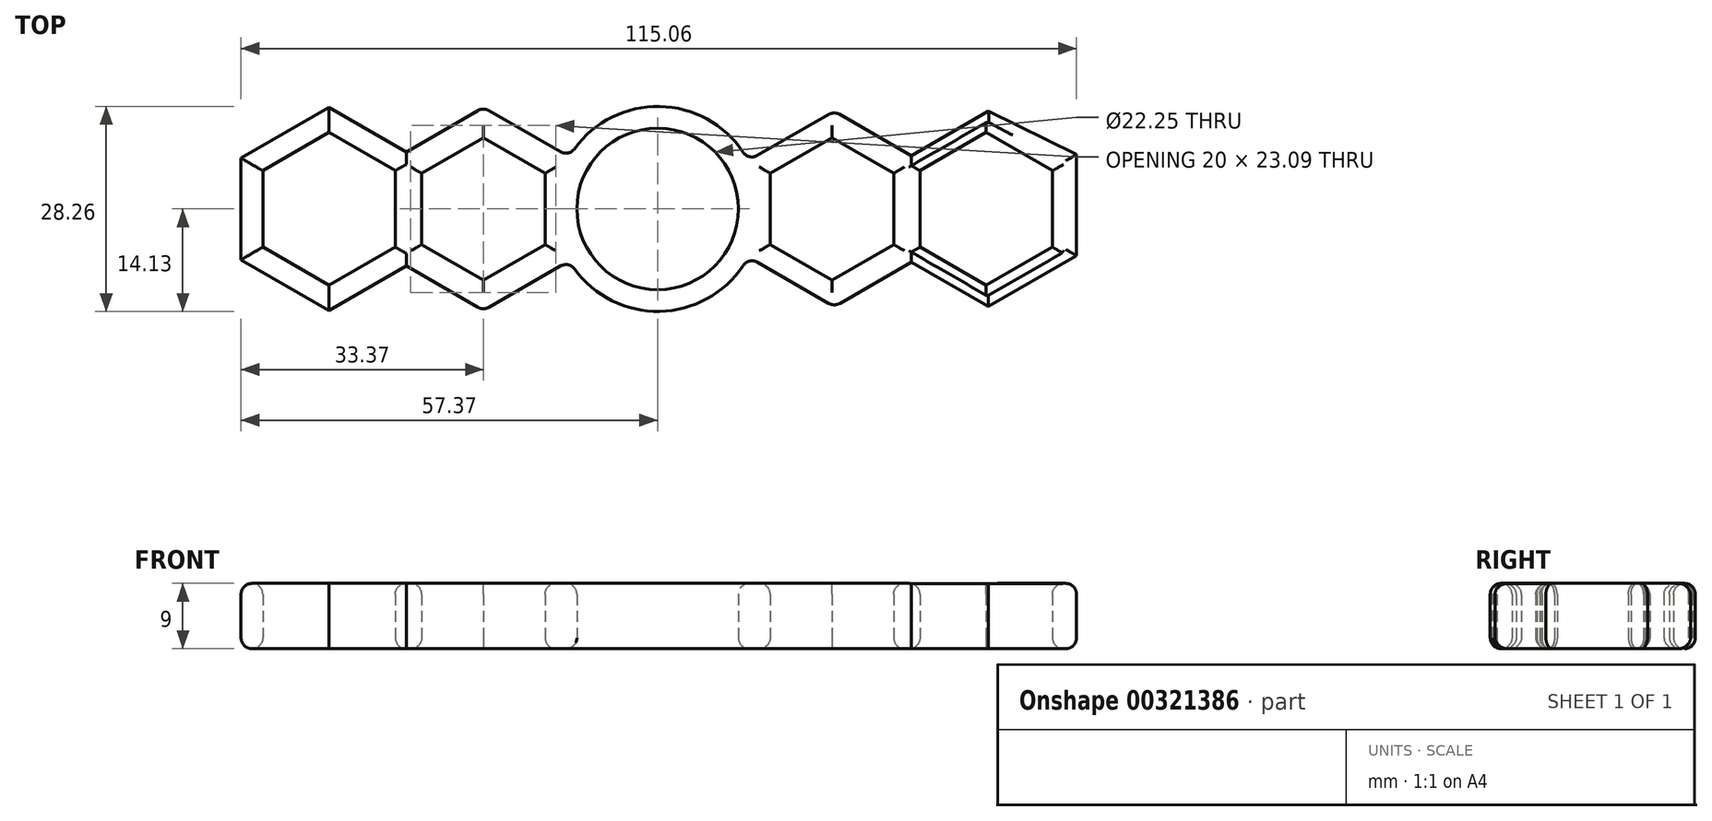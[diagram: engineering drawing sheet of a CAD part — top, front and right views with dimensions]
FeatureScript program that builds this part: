
annotation { "Feature Type Name" : "Feature", "Feature Type Description" : "" }
export const myFeature = defineFeature(function(context is Context, id is Id, definition is map)
    precondition{}
    {
        {
            var Q0;
            Q0=qCreatedBy(makeId("Top.planeOp"),FACE);
            var sketch = newSketch(context, id + "F0", { "sketchPlane" : qUnion([Q0])});
            skCircle(sketch, "E0", {"center": v(0, 0) * mm, "radius": 11.12 * mm});
            skCircle(sketch, "E1.cCircle", {"center": v(24, 0) * mm, "radius": 8.5 * mm, "construction": true});
            skLineSegment(sketch, "E1.0", {"start": v(15.5, -4.9) * mm, "end": v(15.5, 4.9) * mm});
            skLineSegment(sketch, "E1.1", {"start": v(15.5, 4.9) * mm, "end": v(24, 9.81) * mm});
            skLineSegment(sketch, "E1.2", {"start": v(24, 9.81) * mm, "end": v(32.5, 4.9) * mm});
            skLineSegment(sketch, "E1.3", {"start": v(32.5, 4.9) * mm, "end": v(32.5, -4.9) * mm});
            skLineSegment(sketch, "E1.4", {"start": v(32.5, -4.9) * mm, "end": v(24, -9.81) * mm});
            skLineSegment(sketch, "E1.5", {"start": v(24, -9.81) * mm, "end": v(15.5, -4.9) * mm});
            skPoint(sketch, "E1.0.midPoint", {"position": v(15.5, 0) * mm});
            skLineSegment(sketch, "E2", {"start": v(0, -8.9) * mm, "end": v(0, 12.72) * mm, "construction": true});
            skLineSegment(sketch, "E3", {"start": v(0, 12.72) * mm, "end": v(0, 9.77) * mm, "construction": true});
            skCircle(sketch, "E4.MirrorC", {"center": v(-24, 0) * mm, "radius": 8.5 * mm, "construction": true});
            skLineSegment(sketch, "E5.MirrorCS", {"start": v(-15.5, 4.9) * mm, "end": v(-24, 9.81) * mm});
            skLineSegment(sketch, "E6.MirrorCS", {"start": v(-32.5, 4.9) * mm, "end": v(-32.5, -4.9) * mm});
            skLineSegment(sketch, "E7.MirrorCS", {"start": v(-15.5, -4.9) * mm, "end": v(-15.5, 4.9) * mm});
            skPoint(sketch, "E8.MirrorP", {"position": v(-15.5, 0) * mm});
            skLineSegment(sketch, "E9.MirrorCS", {"start": v(-24, 9.81) * mm, "end": v(-32.5, 4.9) * mm});
            skLineSegment(sketch, "E10.MirrorCS", {"start": v(-24, -9.81) * mm, "end": v(-15.5, -4.9) * mm});
            skLineSegment(sketch, "E11.MirrorCS", {"start": v(-32.5, -4.9) * mm, "end": v(-24, -9.81) * mm});
            skArc(sketch, "E12.0", {"start": v(12.47, 6.63) * mm, "mid": v(0.31, 14.12) * mm, "end": v(-12.17, 7.17) * mm});
            skLineSegment(sketch, "E13.2", {"start": v(-24, -14) * mm, "end": v(-12.17, -7.17) * mm});
            skLineSegment(sketch, "E13.5", {"start": v(-12.17, 7.17) * mm, "end": v(-24, 14) * mm});
            skLineSegment(sketch, "E14.3", {"start": v(12.47, 6.63) * mm, "end": v(24.31, 13.46) * mm});
            skLineSegment(sketch, "E14.5", {"start": v(24.31, -13.46) * mm, "end": v(12.47, -6.63) * mm});
            skArc(sketch, "E15.trimOffspring", {"start": v(-12.17, -7.17) * mm, "mid": v(0.31, -14.12) * mm, "end": v(12.47, -6.63) * mm});
            skPoint(sketch, "E16", {"position": v(45.25, 0) * mm});
            skCircle(sketch, "E17", {"center": v(45.25, 0) * mm, "radius": 9.12 * mm, "construction": true});
            skCircle(sketch, "E18.cCircle", {"center": v(45.25, 0) * mm, "radius": 9.13 * mm, "construction": true});
            skLineSegment(sketch, "E18.0", {"start": v(54.37, 5.27) * mm, "end": v(54.37, -5.27) * mm});
            skLineSegment(sketch, "E18.1", {"start": v(54.37, -5.27) * mm, "end": v(45.25, -10.54) * mm});
            skLineSegment(sketch, "E18.2", {"start": v(45.25, -10.54) * mm, "end": v(36.12, -5.27) * mm});
            skLineSegment(sketch, "E18.3", {"start": v(36.12, -5.27) * mm, "end": v(36.12, 5.27) * mm});
            skLineSegment(sketch, "E18.4", {"start": v(36.12, 5.27) * mm, "end": v(45.25, 10.54) * mm});
            skLineSegment(sketch, "E18.5", {"start": v(45.25, 10.54) * mm, "end": v(54.37, 5.27) * mm});
            skLineSegment(sketch, "E19", {"start": v(24.31, 13.46) * mm, "end": v(24, 9.81) * mm, "construction": true});
            skLineSegment(sketch, "E20", {"start": v(45.56, -13.46) * mm, "end": v(34.94, -7.33) * mm});
            skLineSegment(sketch, "E21", {"start": v(45.56, 13.46) * mm, "end": v(34.94, 7.33) * mm});
            skPoint(sketch, "E22", {"position": v(57.69, 7.54) * mm});
            skLineSegment(sketch, "E23", {"start": v(57.69, 7.54) * mm, "end": v(45.56, 13.46) * mm});
            skLineSegment(sketch, "E24", {"start": v(57.69, 7.54) * mm, "end": v(57.69, -6.46) * mm});
            skLineSegment(sketch, "E25", {"start": v(57.69, -6.46) * mm, "end": v(45.56, -13.46) * mm});
            skPoint(sketch, "E26", {"position": v(34.94, 7.33) * mm});
            skPoint(sketch, "E27", {"position": v(34.94, -7.33) * mm});
            skLineSegment(sketch, "E28", {"start": v(34.94, 7.33) * mm, "end": v(24.31, 13.46) * mm});
            skLineSegment(sketch, "E29", {"start": v(34.94, -7.33) * mm, "end": v(24.31, -13.46) * mm});
            skPoint(sketch, "E30", {"position": v(-45.25, 0) * mm});
            skCircle(sketch, "E31", {"center": v(-45.25, 0) * mm, "radius": 9.12 * mm, "construction": true});
            skCircle(sketch, "E32.cCircle", {"center": v(-45.25, 0) * mm, "radius": 9.13 * mm, "construction": true});
            skLineSegment(sketch, "E32.0", {"start": v(-36.12, 5.27) * mm, "end": v(-36.12, -5.27) * mm});
            skLineSegment(sketch, "E32.1", {"start": v(-36.12, -5.27) * mm, "end": v(-45.25, -10.54) * mm});
            skLineSegment(sketch, "E32.2", {"start": v(-45.25, -10.54) * mm, "end": v(-54.37, -5.27) * mm});
            skLineSegment(sketch, "E32.3", {"start": v(-54.37, -5.27) * mm, "end": v(-54.37, 5.27) * mm});
            skLineSegment(sketch, "E32.4", {"start": v(-54.37, 5.27) * mm, "end": v(-45.25, 10.54) * mm});
            skLineSegment(sketch, "E32.5", {"start": v(-45.25, 10.54) * mm, "end": v(-36.12, 5.27) * mm});
            skPoint(sketch, "E32.0.midPoint", {"position": v(-36.12, 0) * mm});
            skLineSegment(sketch, "E33", {"start": v(-34.62, 7.87) * mm, "end": v(-45.25, 14) * mm});
            skPoint(sketch, "E34", {"position": v(-57.37, 7) * mm});
            skPoint(sketch, "E35", {"position": v(-57.37, -7) * mm});
            skLineSegment(sketch, "E36", {"start": v(-45.25, 14) * mm, "end": v(-57.37, 7) * mm});
            skLineSegment(sketch, "E37", {"start": v(-57.37, -7) * mm, "end": v(-57.37, 7) * mm});
            skLineSegment(sketch, "E38", {"start": v(-57.37, -7) * mm, "end": v(-45.25, -14) * mm});
            skLineSegment(sketch, "E39", {"start": v(-45.25, -14) * mm, "end": v(-34.62, -7.87) * mm});
            skLineSegment(sketch, "E40", {"start": v(-24, 14) * mm, "end": v(-34.62, 7.87) * mm});
            skLineSegment(sketch, "E41", {"start": v(-24, -14) * mm, "end": v(-34.62, -7.87) * mm});
            skPoint(sketch, "E42", {"position": v(-57.37, 0) * mm});
            skPoint(sketch, "E43", {"position": v(57.69, 0.54) * mm});
            skSolve(sketch);
        }
        {
            var Q0;
            Q0=makeQuery(id+"F0.imprint","IMPRINT",FACE,{"disambiguationData":[TD([[makeQuery(id+"F0.imprint","IMPRINT",EDGE,{"derivedFrom":sQuery(id+"F0.wireOp",EDGE,"E0")}),-1.0]])]});
            extrude(context, id + "F1", {"entities" : qUnion([Q0]), "depth" : 9 * mm});
        }
        {
            var Q0;
            Q0=makeQuery(id+"F1.opExtrude","CAP_EDGE",EDGE,{"disambiguationData":[OSD([sQuery(id+"F0.wireOp",EDGE,"E9.MirrorCS")])],"isStart":false});
            var Q1;
            Q1=makeQuery(id+"F1.opExtrude","CAP_EDGE",EDGE,{"disambiguationData":[OSD([sQuery(id+"F0.wireOp",EDGE,"E6.MirrorCS")])],"isStart":false});
            var Q2;
            Q2=makeQuery(id+"F1.opExtrude","CAP_EDGE",EDGE,{"disambiguationData":[OSD([sQuery(id+"F0.wireOp",EDGE,"E11.MirrorCS")])],"isStart":false});
            var Q3;
            Q3=makeQuery(id+"F1.opExtrude","CAP_EDGE",EDGE,{"disambiguationData":[OSD([sQuery(id+"F0.wireOp",EDGE,"E10.MirrorCS")])],"isStart":false});
            var Q4;
            Q4=makeQuery(id+"F1.opExtrude","CAP_EDGE",EDGE,{"disambiguationData":[OSD([sQuery(id+"F0.wireOp",EDGE,"E7.MirrorCS")])],"isStart":false});
            var Q5;
            Q5=makeQuery(id+"F1.opExtrude","CAP_EDGE",EDGE,{"disambiguationData":[OSD([sQuery(id+"F0.wireOp",EDGE,"E5.MirrorCS")])],"isStart":false});
            var Q6;
            Q6=makeQuery(id+"F1.opExtrude","CAP_EDGE",EDGE,{"disambiguationData":[OSD([sQuery(id+"F0.wireOp",EDGE,"E0")])],"isStart":false});
            var Q7;
            Q7=makeQuery(id+"F1.opExtrude","CAP_EDGE",EDGE,{"disambiguationData":[OSD([sQuery(id+"F0.wireOp",EDGE,"E1.0")])],"isStart":false});
            var Q8;
            Q8=makeQuery(id+"F1.opExtrude","CAP_EDGE",EDGE,{"disambiguationData":[OSD([sQuery(id+"F0.wireOp",EDGE,"E1.1")])],"isStart":false});
            var Q9;
            Q9=makeQuery(id+"F1.opExtrude","CAP_EDGE",EDGE,{"disambiguationData":[OSD([sQuery(id+"F0.wireOp",EDGE,"E1.2")])],"isStart":false});
            var Q10;
            Q10=makeQuery(id+"F1.opExtrude","CAP_EDGE",EDGE,{"disambiguationData":[OSD([sQuery(id+"F0.wireOp",EDGE,"E1.3")])],"isStart":false});
            var Q11;
            Q11=makeQuery(id+"F1.opExtrude","CAP_EDGE",EDGE,{"disambiguationData":[OSD([sQuery(id+"F0.wireOp",EDGE,"E1.4")])],"isStart":false});
            var Q12;
            Q12=makeQuery(id+"F1.opExtrude","CAP_EDGE",EDGE,{"disambiguationData":[OSD([sQuery(id+"F0.wireOp",EDGE,"E1.5")])],"isStart":false});
            var Q13;
            Q13=makeQuery(id+"F1.opExtrude","CAP_EDGE",EDGE,{"disambiguationData":[OSD([sQuery(id+"F0.wireOp",EDGE,"E6.MirrorCS")])],"isStart":true});
            var Q14;
            Q14=makeQuery(id+"F1.opExtrude","CAP_EDGE",EDGE,{"disambiguationData":[OSD([sQuery(id+"F0.wireOp",EDGE,"E11.MirrorCS")])],"isStart":true});
            var Q15;
            Q15=makeQuery(id+"F1.opExtrude","CAP_EDGE",EDGE,{"disambiguationData":[OSD([sQuery(id+"F0.wireOp",EDGE,"E10.MirrorCS")])],"isStart":true});
            var Q16;
            Q16=makeQuery(id+"F1.opExtrude","CAP_EDGE",EDGE,{"disambiguationData":[OSD([sQuery(id+"F0.wireOp",EDGE,"E7.MirrorCS")])],"isStart":true});
            var Q17;
            Q17=makeQuery(id+"F1.opExtrude","CAP_EDGE",EDGE,{"disambiguationData":[OSD([sQuery(id+"F0.wireOp",EDGE,"E5.MirrorCS")])],"isStart":true});
            var Q18;
            Q18=makeQuery(id+"F1.opExtrude","CAP_EDGE",EDGE,{"disambiguationData":[OSD([sQuery(id+"F0.wireOp",EDGE,"E9.MirrorCS")])],"isStart":true});
            var Q19;
            Q19=makeQuery(id+"F1.opExtrude","CAP_EDGE",EDGE,{"disambiguationData":[OSD([sQuery(id+"F0.wireOp",EDGE,"E0")])],"isStart":true});
            var Q20;
            Q20=makeQuery(id+"F1.opExtrude","CAP_EDGE",EDGE,{"disambiguationData":[OSD([sQuery(id+"F0.wireOp",EDGE,"E1.0")])],"isStart":true});
            var Q21;
            Q21=makeQuery(id+"F1.opExtrude","CAP_EDGE",EDGE,{"disambiguationData":[OSD([sQuery(id+"F0.wireOp",EDGE,"E1.5")])],"isStart":true});
            var Q22;
            Q22=makeQuery(id+"F1.opExtrude","CAP_EDGE",EDGE,{"disambiguationData":[OSD([sQuery(id+"F0.wireOp",EDGE,"E1.4")])],"isStart":true});
            var Q23;
            Q23=makeQuery(id+"F1.opExtrude","CAP_EDGE",EDGE,{"disambiguationData":[OSD([sQuery(id+"F0.wireOp",EDGE,"E1.3")])],"isStart":true});
            var Q24;
            Q24=makeQuery(id+"F1.opExtrude","CAP_EDGE",EDGE,{"disambiguationData":[OSD([sQuery(id+"F0.wireOp",EDGE,"E1.2")])],"isStart":true});
            var Q25;
            Q25=makeQuery(id+"F1.opExtrude","CAP_EDGE",EDGE,{"disambiguationData":[OSD([sQuery(id+"F0.wireOp",EDGE,"E1.1")])],"isStart":true});
            var Q26;
            Q26=makeQuery(id+"F1.opExtrude","CAP_FACE",FACE,{"disambiguationData":[OSD([sQuery(id+"F0.wireOp",EDGE,"E0"),sQuery(id+"F0.wireOp",EDGE,"E1.0"),sQuery(id+"F0.wireOp",EDGE,"E1.1"),sQuery(id+"F0.wireOp",EDGE,"E1.2"),sQuery(id+"F0.wireOp",EDGE,"E1.3"),sQuery(id+"F0.wireOp",EDGE,"E1.4"),sQuery(id+"F0.wireOp",EDGE,"E1.5"),sQuery(id+"F0.wireOp",EDGE,"E5.MirrorCS"),sQuery(id+"F0.wireOp",EDGE,"E6.MirrorCS"),sQuery(id+"F0.wireOp",EDGE,"E7.MirrorCS"),sQuery(id+"F0.wireOp",EDGE,"E9.MirrorCS"),sQuery(id+"F0.wireOp",EDGE,"E10.MirrorCS"),sQuery(id+"F0.wireOp",EDGE,"E11.MirrorCS"),sQuery(id+"F0.wireOp",EDGE,"E12.0"),sQuery(id+"F0.wireOp",EDGE,"E13.0"),sQuery(id+"F0.wireOp",EDGE,"E13.1"),sQuery(id+"F0.wireOp",EDGE,"E13.2"),sQuery(id+"F0.wireOp",EDGE,"E13.3"),sQuery(id+"F0.wireOp",EDGE,"E13.5"),sQuery(id+"F0.wireOp",EDGE,"E14.1"),sQuery(id+"F0.wireOp",EDGE,"E14.2"),sQuery(id+"F0.wireOp",EDGE,"E14.3"),sQuery(id+"F0.wireOp",EDGE,"E14.4"),sQuery(id+"F0.wireOp",EDGE,"E14.5"),sQuery(id+"F0.wireOp",EDGE,"E15.trimOffspring")])],"isStart":true});
            var Q27;
            Q27=makeQuery(id+"F1.opExtrude","CAP_FACE",FACE,{"disambiguationData":[OSD([sQuery(id+"F0.wireOp",EDGE,"E0"),sQuery(id+"F0.wireOp",EDGE,"E1.0"),sQuery(id+"F0.wireOp",EDGE,"E1.1"),sQuery(id+"F0.wireOp",EDGE,"E1.2"),sQuery(id+"F0.wireOp",EDGE,"E1.3"),sQuery(id+"F0.wireOp",EDGE,"E1.4"),sQuery(id+"F0.wireOp",EDGE,"E1.5"),sQuery(id+"F0.wireOp",EDGE,"E5.MirrorCS"),sQuery(id+"F0.wireOp",EDGE,"E6.MirrorCS"),sQuery(id+"F0.wireOp",EDGE,"E7.MirrorCS"),sQuery(id+"F0.wireOp",EDGE,"E9.MirrorCS"),sQuery(id+"F0.wireOp",EDGE,"E10.MirrorCS"),sQuery(id+"F0.wireOp",EDGE,"E11.MirrorCS"),sQuery(id+"F0.wireOp",EDGE,"E12.0"),sQuery(id+"F0.wireOp",EDGE,"E13.0"),sQuery(id+"F0.wireOp",EDGE,"E13.1"),sQuery(id+"F0.wireOp",EDGE,"E13.2"),sQuery(id+"F0.wireOp",EDGE,"E13.3"),sQuery(id+"F0.wireOp",EDGE,"E13.5"),sQuery(id+"F0.wireOp",EDGE,"E14.1"),sQuery(id+"F0.wireOp",EDGE,"E14.2"),sQuery(id+"F0.wireOp",EDGE,"E14.3"),sQuery(id+"F0.wireOp",EDGE,"E14.4"),sQuery(id+"F0.wireOp",EDGE,"E14.5"),sQuery(id+"F0.wireOp",EDGE,"E15.trimOffspring")])],"isStart":false});
            var Q28;
            Q28=makeQuery(id+"F1.opExtrude","SWEPT_EDGE",EDGE,{"disambiguationData":[OSD([sQuery(id+"F0.wireOp",EDGE,"E13.1"),sQuery(id+"F0.wireOp",EDGE,"E13.2")])]});
            var Q29;
            Q29=makeQuery(id+"F1.opExtrude","SWEPT_EDGE",EDGE,{"disambiguationData":[OSD([sQuery(id+"F0.wireOp",EDGE,"E13.1"),sQuery(id+"F0.wireOp",EDGE,"E13.3")])]});
            var Q30;
            Q30=makeQuery(id+"F1.opExtrude","SWEPT_EDGE",EDGE,{"disambiguationData":[OSD([sQuery(id+"F0.wireOp",EDGE,"E13.2"),sQuery(id+"F0.wireOp",EDGE,"E15.trimOffspring")])]});
            var Q31;
            Q31=makeQuery(id+"F1.opExtrude","SWEPT_EDGE",EDGE,{"disambiguationData":[OSD([sQuery(id+"F0.wireOp",EDGE,"E14.5"),sQuery(id+"F0.wireOp",EDGE,"E15.trimOffspring")])]});
            var Q32;
            Q32=makeQuery(id+"F1.opExtrude","SWEPT_EDGE",EDGE,{"disambiguationData":[OSD([sQuery(id+"F0.wireOp",EDGE,"E14.4"),sQuery(id+"F0.wireOp",EDGE,"E14.5")])]});
            var Q33;
            Q33=makeQuery(id+"F1.opExtrude","SWEPT_EDGE",EDGE,{"disambiguationData":[OSD([sQuery(id+"F0.wireOp",EDGE,"E14.2"),sQuery(id+"F0.wireOp",EDGE,"E14.4")])]});
            var Q34;
            Q34=makeQuery(id+"F1.opExtrude","SWEPT_EDGE",EDGE,{"disambiguationData":[OSD([sQuery(id+"F0.wireOp",EDGE,"E14.1"),sQuery(id+"F0.wireOp",EDGE,"E14.2")])]});
            var Q35;
            Q35=makeQuery(id+"F1.opExtrude","SWEPT_EDGE",EDGE,{"disambiguationData":[OSD([sQuery(id+"F0.wireOp",EDGE,"E14.1"),sQuery(id+"F0.wireOp",EDGE,"E14.3")])]});
            var Q36;
            Q36=makeQuery(id+"F1.opExtrude","SWEPT_EDGE",EDGE,{"disambiguationData":[OSD([sQuery(id+"F0.wireOp",EDGE,"E12.0"),sQuery(id+"F0.wireOp",EDGE,"E14.3")])]});
            var Q37;
            Q37=makeQuery(id+"F1.opExtrude","SWEPT_EDGE",EDGE,{"disambiguationData":[OSD([sQuery(id+"F0.wireOp",EDGE,"E12.0"),sQuery(id+"F0.wireOp",EDGE,"E13.5")])]});
            var Q38;
            Q38=makeQuery(id+"F1.opExtrude","SWEPT_EDGE",EDGE,{"disambiguationData":[OSD([sQuery(id+"F0.wireOp",EDGE,"E13.0"),sQuery(id+"F0.wireOp",EDGE,"E13.5")])]});
            var Q39;
            Q39=makeQuery(id+"F1.opExtrude","SWEPT_EDGE",EDGE,{"disambiguationData":[OSD([sQuery(id+"F0.wireOp",EDGE,"E13.0"),sQuery(id+"F0.wireOp",EDGE,"E13.3")])]});
            fillet(context, id + "F2", {"entities" : qUnion([Q0, Q1, Q2, Q3, Q4, Q5, Q6, Q7, Q8, Q9, Q10, Q11, Q12, Q13, Q14, Q15, Q16, Q17, Q18, Q19, Q20, Q21, Q22, Q23, Q24, Q25, Q26, Q27, Q28, Q29, Q30, Q31, Q32, Q33, Q34, Q35, Q36, Q37, Q38, Q39]), "radius" : 1.5 * mm, "tangentPropagation" : true, "allowEdgeOverflow" : false});
        }
    });
